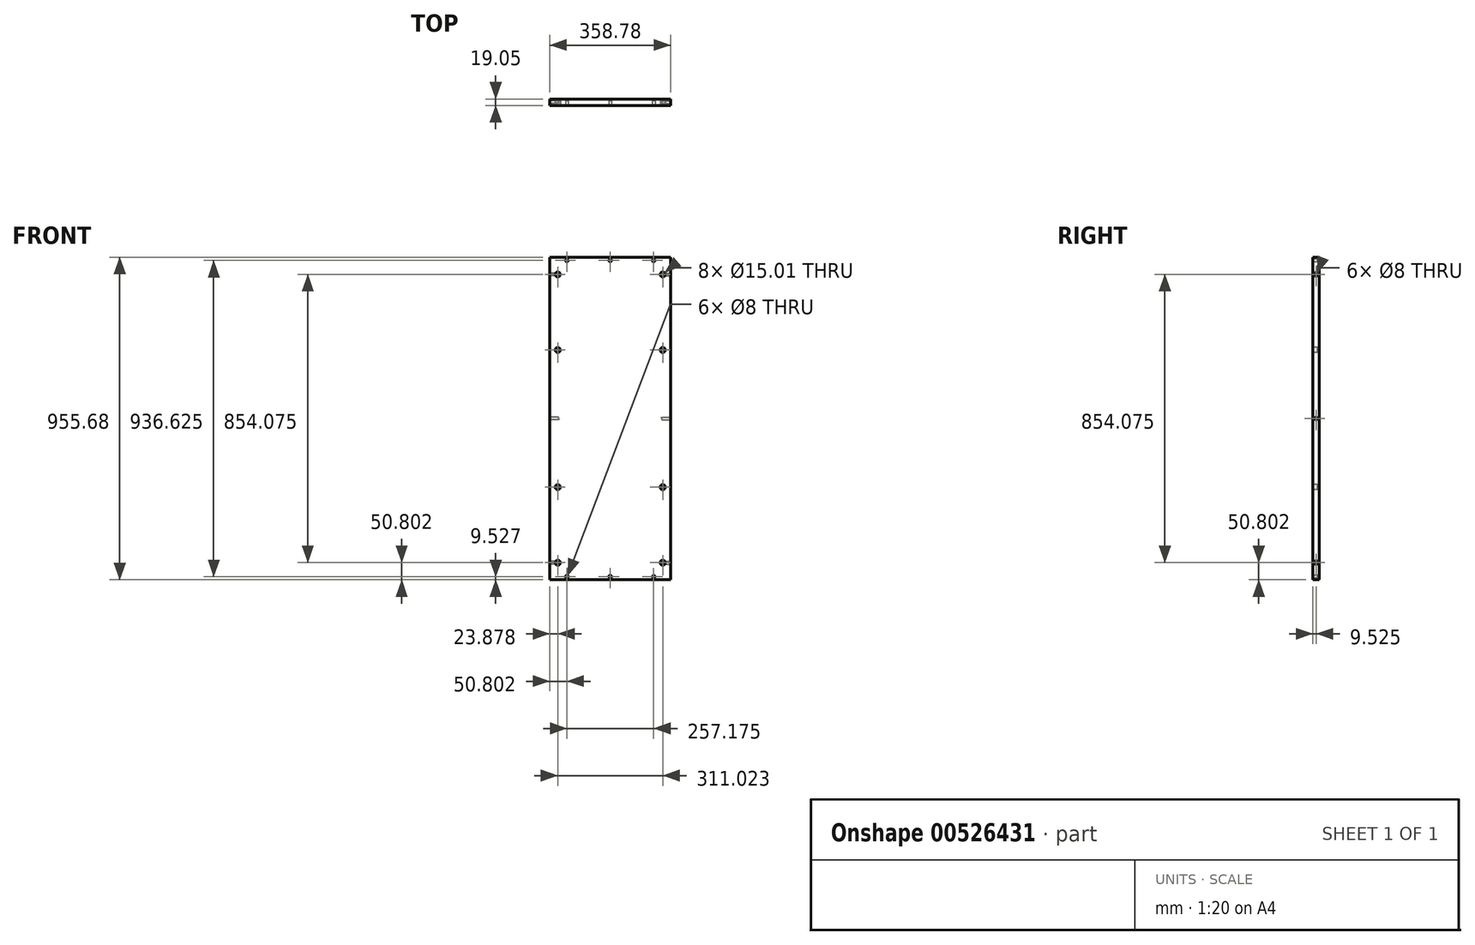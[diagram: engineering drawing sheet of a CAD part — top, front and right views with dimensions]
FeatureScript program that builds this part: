
annotation { "Feature Type Name" : "Feature", "Feature Type Description" : "" }
export const myFeature = defineFeature(function(context is Context, id is Id, definition is map)
    precondition{}
    {
        {
            var Q0;
            Q0=qCreatedBy(makeId("Front.planeOp"),FACE);
            var sketch = newSketch(context, id + "F0", { "sketchPlane" : qUnion([Q0])});
            skLineSegment(sketch, "E0.bottom", {"start": v(179.39, 477.84) * mm, "end": v(-179.39, 477.84) * mm});
            skLineSegment(sketch, "E0.top", {"start": v(179.39, -477.84) * mm, "end": v(-179.39, -477.84) * mm});
            skLineSegment(sketch, "E0.left", {"start": v(179.39, 477.84) * mm, "end": v(179.39, -477.84) * mm});
            skLineSegment(sketch, "E0.right", {"start": v(-179.39, 477.84) * mm, "end": v(-179.39, -477.84) * mm});
            skPoint(sketch, "E0.middle", {"position": v(0, 0) * mm});
            skSolve(sketch);
        }
        {
            var Q0;
            Q0=makeQuery(id+"F0.imprint","IMPRINT",FACE,{"disambiguationData":[TD([[makeQuery(id+"F0.imprint","IMPRINT",EDGE,{"derivedFrom":sQuery(id+"F0.wireOp",EDGE,"E0.bottom")}),1.0]])]});
            extrude(context, id + "F1", {"entities" : qUnion([Q0]), "depth" : 19.05 * mm, "offsetDistance" : 25.4 * mm});
        }
        {
            var Q0;
            Q0=makeQuery(id+"F1.opExtrude","CAP_FACE",FACE,{"disambiguationData":[OSD([sQuery(id+"F0.wireOp",EDGE,"E0.bottom"),sQuery(id+"F0.wireOp",EDGE,"E0.top"),sQuery(id+"F0.wireOp",EDGE,"E0.left"),sQuery(id+"F0.wireOp",EDGE,"E0.right")])],"isStart":false});
            var sketch = newSketch(context, id + "F2", { "sketchPlane" : qUnion([Q0])});
            skLineSegment(sketch, "E1", {"start": v(-179.39, 477.84) * mm, "end": v(-179.39, 468.31) * mm});
            skLineSegment(sketch, "E2", {"start": v(-179.39, 468.31) * mm, "end": v(179.39, 468.31) * mm});
            skLineSegment(sketch, "E3", {"start": v(179.39, 468.31) * mm, "end": v(128.59, 468.31) * mm});
            skLineSegment(sketch, "E4", {"start": v(128.59, 468.31) * mm, "end": v(0, 468.31) * mm});
            skLineSegment(sketch, "E5", {"start": v(-179.39, 468.31) * mm, "end": v(-128.59, 468.31) * mm});
            skLineSegment(sketch, "E6", {"start": v(-179.39, -477.84) * mm, "end": v(-179.39, -468.31) * mm});
            skLineSegment(sketch, "E7", {"start": v(-179.39, -468.31) * mm, "end": v(179.39, -468.31) * mm});
            skLineSegment(sketch, "E8", {"start": v(179.39, -468.31) * mm, "end": v(128.59, -468.31) * mm});
            skLineSegment(sketch, "E9", {"start": v(-179.39, -468.31) * mm, "end": v(-128.59, -468.31) * mm});
            skLineSegment(sketch, "E10", {"start": v(-179.39, -468.31) * mm, "end": v(0, -468.31) * mm});
            skPoint(sketch, "E11", {"position": v(-128.59, 468.31) * mm});
            skPoint(sketch, "E12", {"position": v(0, 468.31) * mm});
            skPoint(sketch, "E13", {"position": v(128.59, 468.31) * mm});
            skPoint(sketch, "E14", {"position": v(-128.59, -468.31) * mm});
            skPoint(sketch, "E15", {"position": v(0, -468.31) * mm});
            skPoint(sketch, "E16", {"position": v(128.59, -468.31) * mm});
            skSolve(sketch);
        }
        {
            var Q0;
            Q0=sQuery(id+"F2.wireOp",VERTEX,"E12");
            var Q1;
            Q1=sQuery(id+"F2.wireOp",VERTEX,"E11");
            var Q2;
            Q2=sQuery(id+"F2.wireOp",VERTEX,"E13");
            var Q3;
            Q3=sQuery(id+"F2.wireOp",VERTEX,"E14");
            var Q4;
            Q4=sQuery(id+"F2.wireOp",VERTEX,"E16");
            var Q5;
            Q5=makeQuery(id+"F1.opExtrude","SWEPT_BODY",BODY,{"disambiguationData":[OSD([sQuery(id+"F0.wireOp",EDGE,"E0.bottom"),sQuery(id+"F0.wireOp",EDGE,"E0.top"),sQuery(id+"F0.wireOp",EDGE,"E0.left"),sQuery(id+"F0.wireOp",EDGE,"E0.right")])]});
            hole(context, id + "F3", {"style" : HoleStyle.SIMPLE, "endStyle" : HoleEndStyle.BLIND, "holeDiameter" : 8 * mm, "holeDepth" : 14.22 * mm, "isTappedThrough" : true, "tappedDepth" : 12.7 * mm, "tapClearance" : 3, "startFromSketch" : true, "locations" : qUnion([Q0, Q1, Q2, Q3, Q4]), "scope" : qUnion([Q5])});
        }
        {
            var Q0;
            Q0=sQuery(id+"F2.wireOp",VERTEX,"E15");
            var Q1;
            Q1=makeQuery(id+"F1.opExtrude","SWEPT_BODY",BODY,{"disambiguationData":[OSD([sQuery(id+"F0.wireOp",EDGE,"E0.bottom"),sQuery(id+"F0.wireOp",EDGE,"E0.top"),sQuery(id+"F0.wireOp",EDGE,"E0.left"),sQuery(id+"F0.wireOp",EDGE,"E0.right")])]});
            hole(context, id + "F4", {"style" : HoleStyle.SIMPLE, "endStyle" : HoleEndStyle.BLIND, "holeDiameter" : 8 * mm, "holeDepth" : 14.22 * mm, "isTappedThrough" : true, "tappedDepth" : 12.7 * mm, "tapClearance" : 3, "startFromSketch" : true, "locations" : qUnion([Q0]), "scope" : qUnion([Q1])});
        }
        {
            var Q0;
            Q0=makeQuery(id+"F1.opExtrude","CAP_FACE",FACE,{"disambiguationData":[OSD([sQuery(id+"F0.wireOp",EDGE,"E0.bottom"),sQuery(id+"F0.wireOp",EDGE,"E0.top"),sQuery(id+"F0.wireOp",EDGE,"E0.left"),sQuery(id+"F0.wireOp",EDGE,"E0.right")])],"isStart":false});
            var sketch = newSketch(context, id + "F5", { "sketchPlane" : qUnion([Q0])});
            skLineSegment(sketch, "E17", {"start": v(-179.39, 477.84) * mm, "end": v(-155.51, 477.84) * mm});
            skLineSegment(sketch, "E18", {"start": v(-155.51, 477.84) * mm, "end": v(-155.51, -477.84) * mm});
            skLineSegment(sketch, "E19", {"start": v(-155.51, -477.84) * mm, "end": v(-155.51, -427.04) * mm});
            skLineSegment(sketch, "E20", {"start": v(-155.51, 477.84) * mm, "end": v(-155.51, 427.04) * mm});
            skLineSegment(sketch, "E21", {"start": v(-179.39, 0) * mm, "end": v(-155.51, 0) * mm});
            skLineSegment(sketch, "E22", {"start": v(179.39, 477.84) * mm, "end": v(155.51, 477.84) * mm});
            skLineSegment(sketch, "E23", {"start": v(155.51, 477.84) * mm, "end": v(155.51, -477.84) * mm});
            skLineSegment(sketch, "E24", {"start": v(155.51, -477.84) * mm, "end": v(155.51, -427.04) * mm});
            skLineSegment(sketch, "E25", {"start": v(155.51, 477.84) * mm, "end": v(155.51, 427.04) * mm});
            skLineSegment(sketch, "E26", {"start": v(179.39, 0) * mm, "end": v(155.51, 0) * mm});
            skPoint(sketch, "E27", {"position": v(-155.51, 427.04) * mm});
            skPoint(sketch, "E28", {"position": v(155.51, 427.04) * mm});
            skPoint(sketch, "E29", {"position": v(155.51, 0) * mm});
            skPoint(sketch, "E30", {"position": v(-155.51, 0) * mm});
            skPoint(sketch, "E31", {"position": v(-155.51, -427.04) * mm});
            skPoint(sketch, "E32", {"position": v(155.51, -427.04) * mm});
            skLineSegment(sketch, "E33", {"start": v(155.51, 0) * mm, "end": v(155.51, 203.2) * mm});
            skLineSegment(sketch, "E34", {"start": v(155.51, 203.2) * mm, "end": v(-155.51, 203.2) * mm});
            skLineSegment(sketch, "E35", {"start": v(-155.51, 203.2) * mm, "end": v(-155.51, -203.2) * mm});
            skLineSegment(sketch, "E36", {"start": v(-155.51, -203.2) * mm, "end": v(155.51, -203.2) * mm});
            skPoint(sketch, "E37", {"position": v(-155.51, 203.2) * mm});
            skPoint(sketch, "E38", {"position": v(155.51, 203.2) * mm});
            skPoint(sketch, "E39", {"position": v(155.51, -203.2) * mm});
            skPoint(sketch, "E40", {"position": v(-155.51, -203.2) * mm});
            skSolve(sketch);
        }
        {
            var Q0;
            Q0=sQuery(id+"F5.wireOp",VERTEX,"E27");
            var Q1;
            Q1=sQuery(id+"F5.wireOp",VERTEX,"E28");
            var Q2;
            Q2=sQuery(id+"F5.wireOp",VERTEX,"E31");
            var Q3;
            Q3=sQuery(id+"F5.wireOp",VERTEX,"E32");
            var Q4;
            Q4=sQuery(id+"F5.wireOp",VERTEX,"E37");
            var Q5;
            Q5=sQuery(id+"F5.wireOp",VERTEX,"E38");
            var Q6;
            Q6=sQuery(id+"F5.wireOp",VERTEX,"E39");
            var Q7;
            Q7=sQuery(id+"F5.wireOp",VERTEX,"E40");
            var Q8;
            Q8=makeQuery(id+"F1.opExtrude","SWEPT_BODY",BODY,{"disambiguationData":[OSD([sQuery(id+"F0.wireOp",EDGE,"E0.bottom"),sQuery(id+"F0.wireOp",EDGE,"E0.top"),sQuery(id+"F0.wireOp",EDGE,"E0.left"),sQuery(id+"F0.wireOp",EDGE,"E0.right")])]});
            hole(context, id + "F6", {"style" : HoleStyle.SIMPLE, "endStyle" : HoleEndStyle.BLIND, "holeDiameter" : 15 * mm, "holeDepth" : 14.22 * mm, "isTappedThrough" : true, "tappedDepth" : 12.7 * mm, "tapClearance" : 3, "startFromSketch" : true, "locations" : qUnion([Q0, Q1, Q2, Q3, Q4, Q5, Q6, Q7]), "scope" : qUnion([Q8])});
        }
        {
            var Q0;
            Q0=makeQuery(id+"F1.opExtrude","SWEPT_FACE",FACE,{"disambiguationData":[OSD([sQuery(id+"F0.wireOp",EDGE,"E0.left")])]});
            var sketch = newSketch(context, id + "F7", { "sketchPlane" : qUnion([Q0])});
            skLineSegment(sketch, "E41", {"start": v(-9.53, 477.84) * mm, "end": v(-9.53, 427.04) * mm});
            skPoint(sketch, "E41.endSnap0", {"position": v(-9.53, 477.84) * mm});
            skLineSegment(sketch, "E42", {"start": v(-9.53, -477.84) * mm, "end": v(-9.53, -427.04) * mm});
            skLineSegment(sketch, "E43", {"start": v(-19.05, 0) * mm, "end": v(0, 0) * mm});
            skPoint(sketch, "E44", {"position": v(-9.53, 427.04) * mm});
            skPoint(sketch, "E45", {"position": v(-9.53, 0) * mm});
            skPoint(sketch, "E46", {"position": v(-9.53, -427.04) * mm});
            skSolve(sketch);
        }
        {
            var Q0;
            Q0=sQuery(id+"F7.wireOp",VERTEX,"E44");
            var Q1;
            Q1=sQuery(id+"F7.wireOp",VERTEX,"E45");
            var Q2;
            Q2=sQuery(id+"F7.wireOp",VERTEX,"E46");
            var Q3;
            Q3=makeQuery(id+"F1.opExtrude","SWEPT_BODY",BODY,{"disambiguationData":[OSD([sQuery(id+"F0.wireOp",EDGE,"E0.bottom"),sQuery(id+"F0.wireOp",EDGE,"E0.top"),sQuery(id+"F0.wireOp",EDGE,"E0.left"),sQuery(id+"F0.wireOp",EDGE,"E0.right")])]});
            hole(context, id + "F8", {"style" : HoleStyle.SIMPLE, "endStyle" : HoleEndStyle.BLIND, "holeDiameter" : 8 * mm, "holeDepth" : 25.4 * mm, "isTappedThrough" : true, "tappedDepth" : 12.7 * mm, "tapClearance" : 3, "startFromSketch" : true, "locations" : qUnion([Q0, Q1, Q2]), "scope" : qUnion([Q3])});
        }
        {
            var Q0;
            Q0=makeQuery(id+"F1.opExtrude","SWEPT_FACE",FACE,{"disambiguationData":[OSD([sQuery(id+"F0.wireOp",EDGE,"E0.right")])]});
            var sketch = newSketch(context, id + "F9", { "sketchPlane" : qUnion([Q0])});
            skLineSegment(sketch, "E47", {"start": v(9.53, 477.84) * mm, "end": v(9.53, -477.84) * mm});
            skLineSegment(sketch, "E48", {"start": v(9.53, -477.84) * mm, "end": v(9.53, -427.04) * mm});
            skLineSegment(sketch, "E49", {"start": v(9.53, 477.84) * mm, "end": v(9.53, 427.04) * mm});
            skLineSegment(sketch, "E50", {"start": v(19.05, 0) * mm, "end": v(0, 0) * mm});
            skPoint(sketch, "E51", {"position": v(9.53, 427.04) * mm});
            skPoint(sketch, "E52", {"position": v(9.53, -427.04) * mm});
            skPoint(sketch, "E53", {"position": v(9.53, 0) * mm});
            skSolve(sketch);
        }
        {
            var Q0;
            Q0=sQuery(id+"F9.wireOp",VERTEX,"E51");
            var Q1;
            Q1=sQuery(id+"F9.wireOp",VERTEX,"E53");
            var Q2;
            Q2=sQuery(id+"F9.wireOp",VERTEX,"E52");
            var Q3;
            Q3=makeQuery(id+"F1.opExtrude","SWEPT_BODY",BODY,{"disambiguationData":[OSD([sQuery(id+"F0.wireOp",EDGE,"E0.bottom"),sQuery(id+"F0.wireOp",EDGE,"E0.top"),sQuery(id+"F0.wireOp",EDGE,"E0.left"),sQuery(id+"F0.wireOp",EDGE,"E0.right")])]});
            hole(context, id + "F10", {"style" : HoleStyle.SIMPLE, "endStyle" : HoleEndStyle.BLIND, "holeDiameter" : 8 * mm, "holeDepth" : 25.4 * mm, "isTappedThrough" : true, "tappedDepth" : 12.7 * mm, "tapClearance" : 3, "startFromSketch" : true, "locations" : qUnion([Q0, Q1, Q2]), "scope" : qUnion([Q3])});
        }
    });
